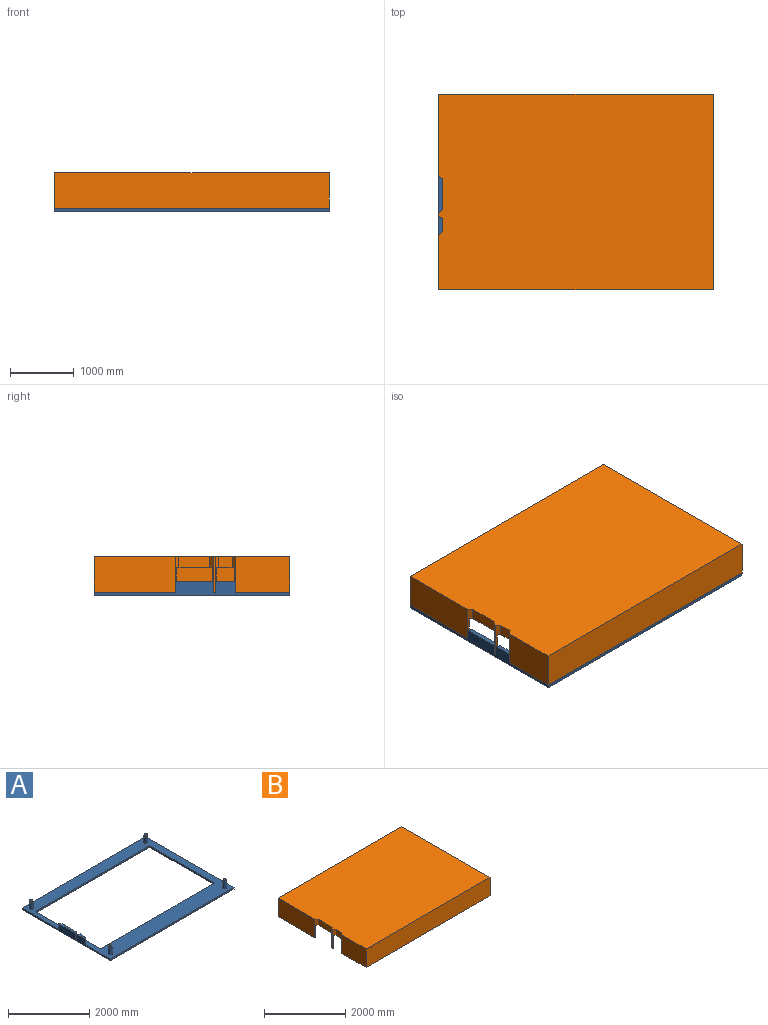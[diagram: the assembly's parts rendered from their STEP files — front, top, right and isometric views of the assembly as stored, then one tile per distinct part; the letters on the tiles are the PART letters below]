
ASSEMBLY  parts=2 mates=1
PART A: 34 faces, bbox 4318x3073.4x284.5 mm
  f0: plane 4318x50.8mm, normal (0,-1,0), area 219354.4mm2, adj f1,f3,f8,f9
  f1: plane 3073.4x50.8mm, normal (1,0,0), area 156128.7mm2, adj f0,f2,f8,f9
  f2: plane 4318x50.8mm, normal (0,1,0), area 219354.4mm2, adj f1,f3,f8,f9
  f3: plane 3073.4x215.9mm, normal (-1,0,0), area 304539.8mm2, adj f0,f2,f8,f9,f26,f27,f29,f30
  f4: plane 3975.1x50.8mm, normal (0,1,0), area 201935.1mm2, adj f5,f7,f8,f9
  f5: plane 2260.6x50.8mm, normal (1,0,0), area 114838.5mm2, adj f4,f6,f8,f9
  f6: plane 3975.1x50.8mm, normal (0,-1,0), area 201935.1mm2, adj f5,f7,f8,f9
  f7: plane 2260.6x50.8mm, normal (-1,0,0), area 114838.5mm2, adj f4,f6,f8,f9
  f8: plane 4318x3073.4mm, normal (0,0,1), area 4201771.3mm2, adj f0,f1,f2,f3,f4,f5,f6,f7
  f9: plane 4318x3073.4mm, normal (0,0,-1), area 4284830.1mm2, adj f0,f1,f2,f3,f4,f5,f6,f7
  f10: cylinder r=37.46mm len=74.93mm, axis (0,0,-1), area 13154.1mm2, adj f11,f13
  f11: plane 74.93x74.93mm, normal (0,0,1), area 4409.6mm2, adj f10
  f12: cylinder r=50.8mm len=177.8mm, axis (0,0,-1), area 56751.2mm2, adj f8,f13
  f13: plane 101.6x101.6mm, normal (0,0,1), area 3697.7mm2, adj f10,f12
  f14: cylinder r=37.46mm len=74.93mm, axis (0,0,-1), area 13154.1mm2, adj f15,f17
  f15: plane 74.93x74.93mm, normal (0,0,1), area 4409.6mm2, adj f14
  f16: cylinder r=50.8mm len=177.8mm, axis (0,0,-1), area 56751.2mm2, adj f8,f17
  f17: plane 101.6x101.6mm, normal (0,0,1), area 3697.7mm2, adj f14,f16
  f18: cylinder r=37.46mm len=74.93mm, axis (0,0,-1), area 13154.1mm2, adj f19,f21
  f19: plane 74.93x74.93mm, normal (0,0,1), area 4409.6mm2, adj f18
  f20: cylinder r=50.8mm len=177.8mm, axis (0,0,-1), area 56751.2mm2, adj f8,f21
  f21: plane 101.6x101.6mm, normal (0,0,1), area 3697.7mm2, adj f18,f20
  f22: cylinder r=37.46mm len=74.93mm, axis (0,0,-1), area 13154.1mm2, adj f23,f25
  f23: plane 74.93x74.93mm, normal (0,0,1), area 4409.6mm2, adj f22
  f24: cylinder r=50.8mm len=177.8mm, axis (0,0,-1), area 56751.2mm2, adj f8,f25
  f25: plane 101.6x101.6mm, normal (0,0,1), area 3697.7mm2, adj f22,f24
  f26: plane 165.1x63.5mm, normal (0.62,0.78,0), area 13425.9mm2, adj f3,f8,f28,f29
  f27: plane 165.1x63.5mm, normal (0.62,-0.78,0), area 13425.9mm2, adj f3,f8,f28,f29
  f28: plane 487.88x165.1mm, normal (1,0,0), area 80549.3mm2, adj f8,f26,f27,f29
  f29: plane 589.48x63.5mm, normal (0,0,1), area 34206.3mm2, adj f3,f26,f27,f28
  f30: plane 165.1x63.5mm, normal (0.62,0.78,0), area 13425.9mm2, adj f3,f8,f32,f33
  f31: plane 165.1x63.5mm, normal (0.62,-0.78,0), area 13425.9mm2, adj f3,f8,f32,f33
  f32: plane 207.83x165.1mm, normal (1,0,0), area 34313.5mm2, adj f8,f30,f31,f33
  f33: plane 309.43x63.5mm, normal (0,0,1), area 16423.3mm2, adj f3,f30,f31,f32
PART B: 37 faces, bbox 4318x3073.4x558.8 mm
  f0: plane 127x82.55mm, normal (0.62,0.78,0), area 13425.9mm2, adj f5,f6,f27,f28
  f1: plane 127x82.55mm, normal (0.62,-0.78,0), area 13425.9mm2, adj f2,f12,f27,f28
  f2: plane 244.46x127mm, normal (1,0,0), area 31046.2mm2, adj f1,f3,f27,f28
  f3: plane 127x64.3mm, normal (0.62,0.78,0), area 10457.2mm2, adj f2,f4,f27,f28
  f4: plane 127x64.3mm, normal (0.62,-0.78,0), area 10457.2mm2, adj f3,f5,f27,f28
  f5: plane 524.51x127mm, normal (1,0,0), area 66612.2mm2, adj f0,f4,f27,f28
  f6: plane 1276.99x508mm, normal (1,0,0), area 642511.8mm2, adj f0,f8,f9,f18,f27,f28
  f7: plane 1280.8x558.8mm, normal (-1,0,0), area 715708.2mm2, adj f8,f17,f18,f26
  f8: plane 558.8x63.5mm, normal (-0.62,-0.78,0), area 23753.5mm2, adj f6,f7,f18,f24,f26,f27
  f9: plane 4279.9x508mm, normal (0,-1,0), area 2174189.2mm2, adj f6,f10,f18,f28
  f10: plane 3035.3x508mm, normal (-1,0,0), area 1541932.4mm2, adj f9,f11,f18,f28
  f11: plane 4279.9x508mm, normal (0,1,0), area 2174189.2mm2, adj f10,f12,f18,f28
  f12: plane 851.98x508mm, normal (1,0,0), area 426609.6mm2, adj f1,f11,f13,f18,f27,f28
  f13: plane 558.8x63.5mm, normal (-0.62,0.78,0), area 23753.5mm2, adj f12,f14,f18,f25,f26,f27
  f14: plane 855.79x558.8mm, normal (-1,0,0), area 478215.8mm2, adj f13,f15,f18,f26
  f15: plane 4318x558.8mm, normal (0,-1,0), area 2412898.4mm2, adj f14,f16,f18,f26
  f16: plane 3073.4x558.8mm, normal (1,0,0), area 1717415.9mm2, adj f15,f17,f18,f26
  f17: plane 4318x558.8mm, normal (0,1,0), area 2412898.4mm2, adj f7,f16,f18,f26
  f18: plane 4318x3073.4mm, normal (0,0,-1), area 262604.7mm2, adj f6,f7,f8,f9,f10,f11,f12,f13
  f19: plane 381x68.38mm, normal (1,0,0), area 26052.1mm2, adj f20,f22,f23,f27
  f20: plane 558.8x63.5mm, normal (-0.62,0.78,0), area 23753.5mm2, adj f19,f21,f23,f24,f26,f27
  f21: plane 558.8x37.9mm, normal (-1,0,0), area 21177.5mm2, adj f20,f22,f23,f26
  f22: plane 558.8x63.5mm, normal (-0.62,-0.78,0), area 23753.5mm2, adj f19,f21,f23,f25,f26,f27
  f23: plane 68.38x19.05mm, normal (0,0,-1), area 1012.3mm2, adj f19,f20,f21,f22
  f24: plane 487.88x177.8mm, normal (-1,0,0), area 86745.4mm2, adj f8,f20,f26,f27
  f25: plane 207.83x177.8mm, normal (-1,0,0), area 36953mm2, adj f13,f22,f26,f27
  f26: plane 4318x3073.4mm, normal (0,0,1), area 13220311.6mm2, adj f7,f8,f13,f14,f15,f16,f17,f20
  f27: plane 1003.92x82.55mm, normal (0,0,-1), area 40028.7mm2, adj f0,f1,f2,f3,f4,f5,f6,f8
  f28: plane 4279.9x3035.3mm, normal (0,0,-1), area 12884236.6mm2, adj f0,f1,f2,f3,f4,f5,f6,f9
  f29: cylinder r=50.8mm len=274.32mm, axis (0,0,1), area 87559.1mm2, adj f28,f30
  f30: plane 101.6x101.6mm, normal (0,0,-1), area 8107.3mm2, adj f29
  f31: cylinder r=50.8mm len=274.32mm, axis (0,0,1), area 87559.1mm2, adj f28,f32
  f32: plane 101.6x101.6mm, normal (0,0,-1), area 8107.3mm2, adj f31
  f33: cylinder r=50.8mm len=274.32mm, axis (0,0,1), area 87559.1mm2, adj f28,f34
  f34: plane 101.6x101.6mm, normal (0,0,-1), area 8107.3mm2, adj f33
  f35: cylinder r=50.8mm len=274.32mm, axis (0,0,1), area 87559.1mm2, adj f28,f36
  f36: plane 101.6x101.6mm, normal (0,0,-1), area 8107.3mm2, adj f35
PLACE A t=(-216.29,672.01,-1332.47)mm
PLACE B t=(-1634.45,483.67,-773.67)mm
MATE fastened A.f14 <-> B.f31  axis (0,0,1) through (-2212.09,-702.13,-1047.99)mm
